# Revit family: 1
name_source: partatom
category: Lighting Fixtures
revit_build: Autodesk Revit 2016 (Build: 20150220_1215(x64)
units: mm (PartAtom-declared; Revit-internal decimal feet)

## family parameters
Cut with Voids When Loaded = No
Host = Face
Light Source = No
OmniClass Number = 23.80.70.00
OmniClass Title = Lighting
Part Type = Normal
Room Calculation Point = No
Round Connector Dimension = Use Diameter
Shared = No

## types (1)
- Type 1
    AngleOpeningMINUS_SYL = -55.00°
    AngleOpening_SYL = 55.00°
    Apparent Load = 2 VA
    Assembly Code = D5020200
    AssetType = Fixed
    ClassificationName = Uniclass2015
    ClassificationValue = EF_70_80
    Cost = 0 $
    Default Elevation = 1219 mm
    Description = Round recessed wall luminaireCorrosion resistant anodized aluminum, 67lm, 1.5W, 45lm/W, 4000K, CRI80+, non dimmable, IP68, IK10, (ØxD) Ø45x75mm, 3 step MacAdam ellipse, class III, 12-24V-DC, A++ A+ A
    DocumentationLiterature = http://www.sylvania-lighting.com
    DurationUnit = hours
    ElectricShockClassification = Class III
    EmittionSurface_SYL = 28 mm
    ExpectedLife = 50000
    HeightDome_SYL = 20 mm  [stored 0.0656168 ft]
    HieghtGround_SYL = 75 mm
    IfcExportAs = IfcLightFixtureType
    IfcExportType = IfcLightFixtureType
    ImpactProtectionIndex = IK10
    IngressProtection = IP68
    Keynote = 16500
    Lamp = LED
    LampColourRenderingIndex = 80
    LampColourTemperature = 4000 K
    LampNominalLuminous = 67 lm
    LampsType = LED
    LightOutputRatio = 100
    LuminousEfficacy = 44.66 lm/W
    Manufacturer = Feilo Sylvania
    ManufacturerName = Feilo Sylvania
    Material = corrosion resistant anodized aluminum housing, tempered safety glass diffuser
    Material_1_SYL = Aluminum 6061 T6 80 Hot Formed
    Material_2_SYL = PC-Sylvania-PatheDM-Glow
    Material_3_SYL = <By Category>
    Material_4_SYL = <By Category>
    Model = PATHE/WALL/ROUND1 67LM LED 4K
    ModelNumber = 4068691
    ModelReference = PATHE/WALL/ROUND1 67LM LED 4K
    Name = PATHE/WALL/ROUND1 67LM LED 4K
    NominalDepth = 0 mm  [stored 0 ft]
    NominalHeight = 75 mm
    NominalLength = 45 mm
    Offset_SYL = 0 mm  [stored 0 ft]
    PowerConsumption = 1.5 W
    PowerFactor = 0
    RadiusDiffuserBottom_SYL = 34 mm
    RadiusDome_SYL = 71 mm
    RadiusOpeningTop_SYL = 20 mm  [stored 0.0656168 ft]
    RadiusRef_SYL = 60 mm
    Radius_SYL = 48 mm
    Type Image = <None>
    TypeLight_SYL = Pathe DM light : 4069478 PATHE/G/DM3 ELLIP 320LM LED 4K
    TypeName = PATHE/WALL/ROUND1 67LM LED 4K
    URL = http://www.sylvania-lighting.com
    Voltage = 0 V
    Weight = 0.235 kg

note: [stored X ft] marks values corroborated as IEEE doubles in the binary element streams (Revit-internal decimal feet)

## geometry (parser evidence)
native form markers: Blend x4, Sweep x5
no freeform markers — native parametric forms only
